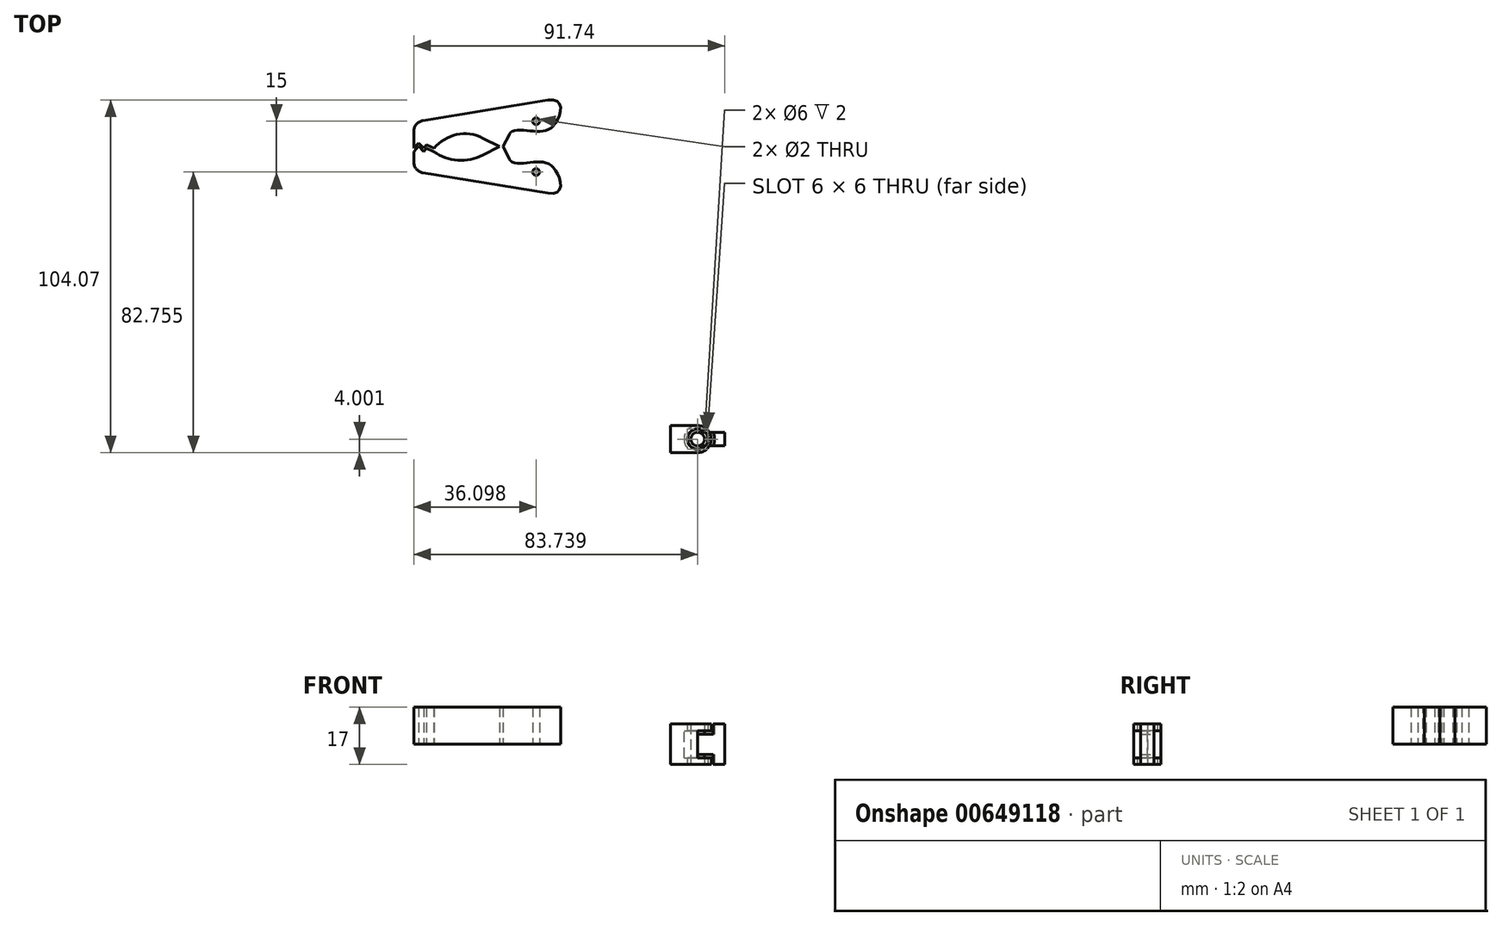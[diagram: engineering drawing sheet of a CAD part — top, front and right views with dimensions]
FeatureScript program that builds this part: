
annotation { "Feature Type Name" : "Feature", "Feature Type Description" : "" }
export const myFeature = defineFeature(function(context is Context, id is Id, definition is map)
    precondition{}
    {
        {
            var Q0;
            Q0=qCreatedBy(makeId("Top.planeOp"),FACE);
            var sketch = newSketch(context, id + "F0", { "sketchPlane" : qUnion([Q0])});
            skLineSegment(sketch, "E0.left", {"start": v(-16.53, 12.52) * mm, "end": v(-16.53, 12.52) * mm});
            skLineSegment(sketch, "E0.right", {"start": v(-56.54, 60.56) * mm, "end": v(-56.54, 63.56) * mm});
            skPoint(sketch, "E0.middle", {"position": v(-33.55, 63.83) * mm});
            skLineSegment(sketch, "E1.top", {"start": v(-56.54, 58.56) * mm, "end": v(-50.54, 58.56) * mm, "construction": true});
            skLineSegment(sketch, "E1.left", {"start": v(-56.54, 60.56) * mm, "end": v(-56.54, 58.56) * mm});
            skLineSegment(sketch, "E1.right", {"start": v(-56.53, 8.52) * mm, "end": v(-56.53, 8.52) * mm});
            skLineSegment(sketch, "E2", {"start": v(-53.54, 58.56) * mm, "end": v(-55.11, 60.19) * mm});
            skPoint(sketch, "E3.visualSharp", {"position": v(-50.54, 60.56) * mm});
            skPoint(sketch, "E4.visualSharp", {"position": v(-56.54, 65.45) * mm});
            skArc(sketch, "E4.filletArc", {"start": v(-53.81, 66.77) * mm, "mid": v(-55.77, 65.67) * mm, "end": v(-56.54, 63.56) * mm});
            skPoint(sketch, "E5.visualSharp", {"position": v(-10.57, 67.1) * mm});
            skPoint(sketch, "E6.visualSharp", {"position": v(-10.57, 62.2) * mm});
            skLineSegment(sketch, "E7", {"start": v(-33.55, 63.83) * mm, "end": v(-16.68, 69.92) * mm, "construction": true});
            skCircle(sketch, "E8", {"center": v(-20.44, 68.56) * mm, "radius": 1 * mm, "construction": true});
            skLineSegment(sketch, "E9", {"start": v(-36.15, 61.59) * mm, "end": v(-31.23, 59.06) * mm});
            skLineSegment(sketch, "E10", {"start": v(-31.23, 59.06) * mm, "end": v(-30.23, 59.06) * mm, "construction": true});
            skLineSegment(sketch, "E11", {"start": v(-30.23, 59.06) * mm, "end": v(-28.36, 62.7) * mm});
            skLineSegment(sketch, "E12", {"start": v(-62.4, 59.06) * mm, "end": v(9.99, 59.06) * mm, "construction": true});
            skLineSegment(sketch, "E13.MirrorCS", {"start": v(-30.23, 59.06) * mm, "end": v(-28.36, 55.42) * mm});
            skCircle(sketch, "E14.MirrorC", {"center": v(-20.44, 49.56) * mm, "radius": 1 * mm, "construction": true});
            skArc(sketch, "E15.MirrorCS", {"start": v(-53.81, 51.36) * mm, "mid": v(-55.77, 52.46) * mm, "end": v(-56.54, 54.56) * mm});
            skLineSegment(sketch, "E16.MirrorCS", {"start": v(-56.54, 57.56) * mm, "end": v(-56.54, 54.56) * mm});
            skLineSegment(sketch, "E17.MirrorCS", {"start": v(-33.55, 54.3) * mm, "end": v(-16.68, 48.2) * mm, "construction": true});
            skPoint(sketch, "E18.MirrorP", {"position": v(-10.57, 55.92) * mm});
            skPoint(sketch, "E19.MirrorP", {"position": v(-10.57, 51.04) * mm});
            skPoint(sketch, "E20.MirrorP", {"position": v(-56.54, 52.68) * mm});
            skPoint(sketch, "E21.MirrorP", {"position": v(-50.54, 57.56) * mm});
            skPoint(sketch, "E22.visualSharp", {"position": v(-33.21, 60.08) * mm});
            skPoint(sketch, "E23.visualSharp", {"position": v(-33.21, 58.05) * mm});
            skPoint(sketch, "E24.visualSharp", {"position": v(-28.21, 55.13) * mm});
            skArc(sketch, "E24.filletArc", {"start": v(-28.36, 55.42) * mm, "mid": v(-28, 54.93) * mm, "end": v(-27.51, 54.56) * mm});
            skPoint(sketch, "E25.visualSharp", {"position": v(-28.21, 63) * mm});
            skArc(sketch, "E25.filletArc", {"start": v(-27.51, 63.56) * mm, "mid": v(-28, 63.2) * mm, "end": v(-28.36, 62.7) * mm});
            skLineSegment(sketch, "E26", {"start": v(-56.54, 60.56) * mm, "end": v(-49.14, 58.6) * mm, "construction": true});
            skLineSegment(sketch, "E27", {"start": v(-56.54, 58.56) * mm, "end": v(-55.11, 60.19) * mm});
            skLineSegment(sketch, "E28", {"start": v(-53.54, 58.56) * mm, "end": v(-52.84, 59.59) * mm});
            skLineSegment(sketch, "E29", {"start": v(-52.84, 59.59) * mm, "end": v(-50.54, 58.56) * mm});
            skLineSegment(sketch, "E30.top", {"start": v(-56.54, 57.56) * mm, "end": v(-50.54, 57.56) * mm, "construction": true});
            skLineSegment(sketch, "E31", {"start": v(-53.54, 57.56) * mm, "end": v(-55.11, 59.19) * mm});
            skPoint(sketch, "E32.visualSharp", {"position": v(-50.53, 48.52) * mm});
            skLineSegment(sketch, "E33", {"start": v(-56.58, 59.56) * mm, "end": v(-49.08, 57.64) * mm, "construction": true});
            skLineSegment(sketch, "E34", {"start": v(-56.54, 57.56) * mm, "end": v(-55.11, 59.19) * mm});
            skLineSegment(sketch, "E35", {"start": v(-53.54, 57.56) * mm, "end": v(-52.83, 58.6) * mm});
            skLineSegment(sketch, "E36", {"start": v(-52.83, 58.6) * mm, "end": v(-50.65, 57.61) * mm});
            skLineSegment(sketch, "E37", {"start": v(-56.58, 59.56) * mm, "end": v(-56.54, 57.56) * mm, "construction": true});
            skArc(sketch, "E38", {"start": v(-36.15, 61.59) * mm, "mid": v(-43.88, 62.63) * mm, "end": v(-50.54, 58.56) * mm});
            skLineSegment(sketch, "E39", {"start": v(-53.81, 66.77) * mm, "end": v(-17, 72.78) * mm});
            skLineSegment(sketch, "E40.MirrorCS", {"start": v(-53.81, 51.36) * mm, "end": v(-17, 45.35) * mm});
            skLineSegment(sketch, "E41.MirrorCS", {"start": v(-17, 45.35) * mm, "end": v(-17, 45.35) * mm});
            skLineSegment(sketch, "E42.MirrorCS", {"start": v(-36.15, 56.54) * mm, "end": v(-31.23, 59.06) * mm});
            skArc(sketch, "E43", {"start": v(-50.65, 57.61) * mm, "mid": v(-43.55, 55.04) * mm, "end": v(-36.15, 56.54) * mm});
            skLineSegment(sketch, "E44", {"start": v(-20.44, 68.56) * mm, "end": v(-20.44, 49.56) * mm, "construction": true});
            skCircle(sketch, "E45", {"center": v(-20.44, 66.56) * mm, "radius": 1 * mm});
            skFitSpline(sketch, "E46", {"points": [v(-27.51, 63.56) * mm, v(-20.44, 63.56) * mm, v(-14.5, 66.38) * mm, v(-17, 72.78) * mm], "startDerivative": vector(15.1, 7.97) * mm, "endDerivative": vector(-45.53, -7.44) * mm});
            skFitSpline(sketch, "E47.MirrorCS", {"points": [v(-27.51, 54.56) * mm, v(-20.44, 54.56) * mm, v(-14.5, 51.75) * mm, v(-17, 45.35) * mm], "startDerivative": vector(15.1, -7.97) * mm, "endDerivative": vector(-45.53, 7.44) * mm});
            skCircle(sketch, "E48.MirrorC", {"center": v(-20.44, 51.56) * mm, "radius": 1 * mm});
            skSolve(sketch);
        }
        {
            var Q0;
            Q0=makeQuery(id+"F0.imprint","IMPRINT",FACE,{"disambiguationData":[TD([[makeQuery(id+"F0.imprint","IMPRINT",EDGE,{"derivedFrom":sQuery(id+"F0.wireOp",EDGE,"E0.right")}),-1.0]])]});
            extrude(context, id + "F1", {"entities" : qUnion([Q0]), "depth" : 11 * mm, "offsetDistance" : 25 * mm});
        }
        {
            var Q0;
            Q0=qCreatedBy(makeId("Top.planeOp"),FACE);
            var sketch = newSketch(context, id + "F2", { "sketchPlane" : qUnion([Q0])});
            skLineSegment(sketch, "E49.bottom", {"start": v(-19.85, -51.8) * mm, "end": v(-33.85, -51.8) * mm, "construction": true});
            skLineSegment(sketch, "E49.left", {"start": v(-19.85, -51.8) * mm, "end": v(-19.85, -5.8) * mm, "construction": true});
            skLineSegment(sketch, "E49.right", {"start": v(-33.85, -51.8) * mm, "end": v(-33.85, -5.8) * mm, "construction": true});
            skPoint(sketch, "E49.middle", {"position": v(-26.85, -28.8) * mm});
            skCircle(sketch, "E50", {"center": v(-26.85, -25) * mm, "radius": 2 * mm});
            skCircle(sketch, "E51", {"center": v(-26.85, -25) * mm, "radius": 2.1 * mm});
            skCircle(sketch, "E52", {"center": v(-26.85, -25) * mm, "radius": 3.1 * mm});
            skCircle(sketch, "E53", {"center": v(-26.85, -25) * mm, "radius": 3 * mm});
            skCircle(sketch, "E54", {"center": v(-26.85, -25) * mm, "radius": 3.2 * mm, "construction": true});
            skLineSegment(sketch, "E55", {"start": v(-26.85, -21.9) * mm, "end": v(-26.85, -21.8) * mm});
            skLineSegment(sketch, "E56", {"start": v(-26.85, -21.8) * mm, "end": v(-26.78, -28.1) * mm});
            skLineSegment(sketch, "E57", {"start": v(-26.78, -28.1) * mm, "end": v(-26.78, -28.2) * mm});
            skArc(sketch, "E58", {"start": v(-26.78, -28.2) * mm, "mid": v(-23.66, -24.97) * mm, "end": v(-26.85, -21.8) * mm});
            skLineSegment(sketch, "E59", {"start": v(-26.85, -21.8) * mm, "end": v(-26.85, -5.8) * mm, "construction": true});
            skLineSegment(sketch, "E60.bottom", {"start": v(-25.85, -51.8) * mm, "end": v(-27.85, -51.8) * mm, "construction": true});
            skLineSegment(sketch, "E60.top", {"start": v(-25.85, -43.8) * mm, "end": v(-27.85, -43.8) * mm, "construction": true});
            skLineSegment(sketch, "E60.left", {"start": v(-27.85, -51.8) * mm, "end": v(-27.85, -43.8) * mm, "construction": true});
            skLineSegment(sketch, "E60.right", {"start": v(-25.85, -51.8) * mm, "end": v(-25.85, -43.8) * mm, "construction": true});
            skPoint(sketch, "E60.middle", {"position": v(-26.85, -47.8) * mm});
            skLineSegment(sketch, "E61.bottom", {"start": v(-19.85, -21.8) * mm, "end": v(-33.85, -21.8) * mm, "construction": true});
            skLineSegment(sketch, "E61.left", {"start": v(-19.85, -21.8) * mm, "end": v(-19.85, -5.8) * mm, "construction": true});
            skPoint(sketch, "E61.middle", {"position": v(-26.85, -13.8) * mm});
            skLineSegment(sketch, "E62", {"start": v(-37.85, -11.8) * mm, "end": v(-33.85, -11.8) * mm, "construction": true});
            skLineSegment(sketch, "E63", {"start": v(-41.85, -11.8) * mm, "end": v(-37.85, -11.8) * mm, "construction": true});
            skLineSegment(sketch, "E64", {"start": v(-15.85, -11.8) * mm, "end": v(-11.85, -11.8) * mm, "construction": true});
            skLineSegment(sketch, "E65", {"start": v(-19.85, -11.8) * mm, "end": v(-15.85, -11.8) * mm, "construction": true});
            skCircle(sketch, "E66", {"center": v(-37.85, -11.8) * mm, "radius": 1 * mm});
            skCircle(sketch, "E67", {"center": v(-15.85, -11.8) * mm, "radius": 1 * mm});
            skLineSegment(sketch, "E68", {"start": v(-26.85, -43.8) * mm, "end": v(-26.85, -51.8) * mm, "construction": true});
            skLineSegment(sketch, "E69", {"start": v(-33.85, -11.8) * mm, "end": v(-19.85, -11.8) * mm, "construction": true});
            skLineSegment(sketch, "E70.bottom", {"start": v(-33.85, -5.8) * mm, "end": v(-41.85, -5.8) * mm});
            skLineSegment(sketch, "E70.top", {"start": v(-33.85, -51.8) * mm, "end": v(-41.85, -51.8) * mm, "construction": true});
            skLineSegment(sketch, "E70.left", {"start": v(-33.85, -5.8) * mm, "end": v(-33.85, -51.8) * mm, "construction": true});
            skLineSegment(sketch, "E70.right", {"start": v(-41.85, -5.8) * mm, "end": v(-41.85, -51.8) * mm, "construction": true});
            skLineSegment(sketch, "E71.bottom", {"start": v(-19.85, -5.8) * mm, "end": v(-11.85, -5.8) * mm});
            skLineSegment(sketch, "E71.top", {"start": v(-19.85, -52.05) * mm, "end": v(-11.85, -52.05) * mm, "construction": true});
            skLineSegment(sketch, "E71.left", {"start": v(-19.85, -5.8) * mm, "end": v(-19.85, -52.05) * mm, "construction": true});
            skLineSegment(sketch, "E71.right", {"start": v(-11.85, -5.8) * mm, "end": v(-11.85, -52.05) * mm, "construction": true});
            skLineSegment(sketch, "E72", {"start": v(-26.85, -28.8) * mm, "end": v(-26.85, -43.8) * mm, "construction": true});
            skLineSegment(sketch, "E73", {"start": v(-27.85, -51.8) * mm, "end": v(-25.85, -51.8) * mm});
            skLineSegment(sketch, "E74", {"start": v(-25.85, -51.8) * mm, "end": v(-27.85, -49.8) * mm});
            skLineSegment(sketch, "E75", {"start": v(-27.85, -49.8) * mm, "end": v(-25.85, -49.8) * mm});
            skLineSegment(sketch, "E76", {"start": v(-25.85, -49.8) * mm, "end": v(-27.85, -47.8) * mm});
            skLineSegment(sketch, "E77", {"start": v(-27.85, -47.8) * mm, "end": v(-25.85, -47.8) * mm});
            skLineSegment(sketch, "E78", {"start": v(-25.85, -47.8) * mm, "end": v(-27.85, -48.1) * mm});
            skArc(sketch, "E79", {"start": v(-41.85, -37.8) * mm, "mid": v(-37.75, -47.7) * mm, "end": v(-27.85, -51.8) * mm});
            skArc(sketch, "E80", {"start": v(-25.85, -51.8) * mm, "mid": v(-15.96, -47.7) * mm, "end": v(-11.85, -37.8) * mm});
            skLineSegment(sketch, "E81", {"start": v(-41.85, -37.8) * mm, "end": v(-11.85, -37.8) * mm, "construction": true});
            skLineSegment(sketch, "E82", {"start": v(-41.85, -37.8) * mm, "end": v(-41.85, -5.8) * mm});
            skLineSegment(sketch, "E83", {"start": v(-11.85, -37.8) * mm, "end": v(-11.85, -5.8) * mm});
            skLineSegment(sketch, "E84", {"start": v(-33.85, -5.8) * mm, "end": v(-33.85, -21.8) * mm});
            skLineSegment(sketch, "E85", {"start": v(-19.85, -28.48) * mm, "end": v(-19.85, -47.8) * mm});
            skLineSegment(sketch, "E86", {"start": v(-19.85, -47.8) * mm, "end": v(-25.85, -47.8) * mm});
            skLineSegment(sketch, "E87", {"start": v(-19.85, -21.8) * mm, "end": v(-19.85, -5.8) * mm});
            skLineSegment(sketch, "E88", {"start": v(-27.85, -47.8) * mm, "end": v(-33.85, -47.8) * mm});
            skLineSegment(sketch, "E89", {"start": v(-33.85, -47.8) * mm, "end": v(-33.85, -21.8) * mm});
            skLineSegment(sketch, "E90", {"start": v(-33.85, -21.66) * mm, "end": v(-33.88, -21.7) * mm});
            skLineSegment(sketch, "E91", {"start": v(-19.85, -21.8) * mm, "end": v(-26.84, -23) * mm});
            skLineSegment(sketch, "E92", {"start": v(-26.8, -27) * mm, "end": v(-19.85, -28.48) * mm});
            skLineSegment(sketch, "E93", {"start": v(-26.85, -21.9) * mm, "end": v(-33.85, -21.38) * mm});
            skLineSegment(sketch, "E94", {"start": v(-26.78, -28.1) * mm, "end": v(-33.85, -28.8) * mm});
            skLineSegment(sketch, "E95", {"start": v(-26.85, -25) * mm, "end": v(-19.85, -25) * mm, "construction": true});
            skLineSegment(sketch, "E96", {"start": v(-26.85, -25) * mm, "end": v(-33.85, -25) * mm, "construction": true});
            skLineSegment(sketch, "E97", {"start": v(-33.85, -5.8) * mm, "end": v(-26.85, -5.8) * mm, "construction": true});
            skLineSegment(sketch, "E98", {"start": v(-26.85, -5.8) * mm, "end": v(-19.85, -5.8) * mm, "construction": true});
            skLineSegment(sketch, "E99", {"start": v(-26.85, -25) * mm, "end": v(-26.85, -28.8) * mm, "construction": true});
            skLineSegment(sketch, "E100.bottom", {"start": v(13.2, -7.21) * mm, "end": v(19.2, -7.21) * mm, "construction": true});
            skLineSegment(sketch, "E100.top", {"start": v(13.2, -53.95) * mm, "end": v(19.2, -53.95) * mm, "construction": true});
            skLineSegment(sketch, "E100.left", {"start": v(13.2, -7.21) * mm, "end": v(13.2, -53.95) * mm, "construction": true});
            skLineSegment(sketch, "E100.right", {"start": v(19.2, -7.21) * mm, "end": v(19.2, -53.95) * mm, "construction": true});
            skLineSegment(sketch, "E101", {"start": v(13.2, -13.21) * mm, "end": v(19.2, -13.21) * mm, "construction": true});
            skCircle(sketch, "E102", {"center": v(16.2, -13.21) * mm, "radius": 1 * mm});
            skCircle(sketch, "E103", {"center": v(27.2, -27.19) * mm, "radius": 2 * mm});
            skCircle(sketch, "E104", {"center": v(27.2, -27.19) * mm, "radius": 3 * mm});
            skCircle(sketch, "E105", {"center": v(27.2, -27.19) * mm, "radius": 4 * mm});
            skCircle(sketch, "E106", {"center": v(27.2, -27.19) * mm, "radius": 5 * mm});
            skLineSegment(sketch, "E107", {"start": v(27.2, -27.19) * mm, "end": v(19.2, -27.19) * mm, "construction": true});
            skLineSegment(sketch, "E108", {"start": v(27.2, -7.21) * mm, "end": v(27.2, -54.3) * mm, "construction": true});
            skPoint(sketch, "E108.startSnap0", {"position": v(16.2, -7.21) * mm});
            skLineSegment(sketch, "E109.MirrorCS", {"start": v(35.2, -7.21) * mm, "end": v(35.2, -53.95) * mm, "construction": true});
            skLineSegment(sketch, "E110.MirrorCS", {"start": v(41.2, -13.21) * mm, "end": v(35.2, -13.21) * mm, "construction": true});
            skLineSegment(sketch, "E111.MirrorCS", {"start": v(41.2, -7.21) * mm, "end": v(41.2, -53.95) * mm, "construction": true});
            skLineSegment(sketch, "E112.MirrorCS", {"start": v(41.2, -7.21) * mm, "end": v(35.2, -7.21) * mm, "construction": true});
            skCircle(sketch, "E113.MirrorC", {"center": v(38.2, -13.21) * mm, "radius": 1 * mm});
            skLineSegment(sketch, "E114.MirrorCS", {"start": v(41.2, -53.95) * mm, "end": v(35.2, -53.95) * mm, "construction": true});
            skLineSegment(sketch, "E115.MirrorCS", {"start": v(27.2, -27.19) * mm, "end": v(35.2, -27.19) * mm, "construction": true});
            skLineSegment(sketch, "E116", {"start": v(27.2, -25.19) * mm, "end": v(35.2, -25.19) * mm});
            skLineSegment(sketch, "E117.MirrorCS", {"start": v(27.2, -29.19) * mm, "end": v(35.2, -29.19) * mm});
            skLineSegment(sketch, "E118", {"start": v(19.2, -23.19) * mm, "end": v(19.2, -31.19) * mm});
            skLineSegment(sketch, "E119", {"start": v(35.2, -25.19) * mm, "end": v(35.2, -29.19) * mm});
            skLineSegment(sketch, "E120", {"start": v(23.2, -27.19) * mm, "end": v(25.2, -27.19) * mm});
            skLineSegment(sketch, "E121", {"start": v(27.2, -23.19) * mm, "end": v(19.2, -23.19) * mm});
            skLineSegment(sketch, "E122", {"start": v(27.2, -31.19) * mm, "end": v(19.2, -31.19) * mm});
            skSolve(sketch);
        }
        {
            var Q0;
            {var subQ5=sQuery(id+"F2.wireOp",EDGE,"E118");Q0=makeQuery(id+"F2.imprint","IMPRINT",FACE,{"disambiguationData":[TD([[makeQuery(id+"F2.imprint","IMPRINT",EDGE,{"derivedFrom":subQ5}),1.0]])]});}
            var Q1;
            {var subQ0=sQuery(id+"F2.wireOp",EDGE,"B579V9jg-vVpn-PewL-seOk-HfGn0jfsSapa");var subQ1=sQuery(id+"F2.wireOp",EDGE,"E105");var subQ2=makeQuery(id+"F2.imprint","INTERSECT",VERTEX,{"derivedFrom":[subQ1,subQ0]});Q1=makeQuery(id+"F2.imprint","IMPRINT",FACE,{"disambiguationData":[TD([[makeQuery(id+"F2.imprint","IMPRINT",EDGE,{"disambiguationData":[TD([[subQ2,-1.0]])],"derivedFrom":subQ1}),1.0]])]});}
            var Q2;
            {var subQ5=sQuery(id+"F2.wireOp",EDGE,"E116");var subQ7=sQuery(id+"F2.wireOp",EDGE,"E104");var subQ8=makeQuery(id+"F2.imprint","INTERSECT",VERTEX,{"derivedFrom":[subQ7,subQ5]});Q2=makeQuery(id+"F2.imprint","IMPRINT",FACE,{"disambiguationData":[TD([[makeQuery(id+"F2.imprint","IMPRINT",EDGE,{"disambiguationData":[TD([[subQ8,-1.0]])],"derivedFrom":subQ7}),-1.0]])]});}
            var Q3;
            {var subQ0=sQuery(id+"F2.wireOp",EDGE,"E120");Q3=makeQuery(id+"F2.imprint","IMPRINT",FACE,{"disambiguationData":[TD([[makeQuery(id+"F2.imprint","IMPRINT",EDGE,{"derivedFrom":subQ0}),-1.0]])]});}
            var Q4;
            {var subQ0=sQuery(id+"F2.wireOp",EDGE,"E103");var subQ1=makeQuery(id+"F2.imprint","INTERSECT",VERTEX,{"derivedFrom":[subQ0,sQuery(id+"F2.wireOp",EDGE,"E116")]});Q4=makeQuery(id+"F2.imprint","IMPRINT",FACE,{"disambiguationData":[TD([[makeQuery(id+"F2.imprint","IMPRINT",EDGE,{"disambiguationData":[TD([[subQ1,-1.0]])],"derivedFrom":subQ0}),1.0]])]});}
            var Q5;
            {var subQ0=sQuery(id+"F2.wireOp",EDGE,"E105");var subQ8=makeQuery(id+"F2.imprint","INTERSECT",VERTEX,{"derivedFrom":[subQ0,sQuery(id+"F2.wireOp",EDGE,"E120")]});Q5=makeQuery(id+"F2.imprint","IMPRINT",FACE,{"disambiguationData":[TD([[makeQuery(id+"F2.imprint","IMPRINT",EDGE,{"disambiguationData":[TD([[subQ8,1.0]])],"derivedFrom":subQ0}),-1.0]])]});}
            var Q6;
            {var subQ0=sQuery(id+"F2.wireOp",EDGE,"E116");var subQ1=sQuery(id+"F2.wireOp",EDGE,"E104");var subQ2=makeQuery(id+"F2.imprint","INTERSECT",VERTEX,{"derivedFrom":[subQ1,subQ0]});Q6=makeQuery(id+"F2.imprint","IMPRINT",FACE,{"disambiguationData":[TD([[makeQuery(id+"F2.imprint","IMPRINT",EDGE,{"disambiguationData":[TD([[subQ2,1.0]])],"derivedFrom":subQ1}),-1.0]])]});}
            extrude(context, id + "F3", {"entities" : qUnion([Q0, Q1, Q2, Q3, Q4, Q5, Q6]), "endBound" : BoundingType.SYMMETRIC, "depth" : 12 * mm, "offsetDistance" : 25 * mm});
        }
        {
            var Q0;
            {var subQ4=sQuery(id+"F2.wireOp",EDGE,"E104");var subQ8=makeQuery(id+"F2.imprint","INTERSECT",VERTEX,{"derivedFrom":[subQ4,sQuery(id+"F2.wireOp",EDGE,"E120")]});Q0=makeQuery(id+"F2.imprint","IMPRINT",FACE,{"disambiguationData":[TD([[makeQuery(id+"F2.imprint","IMPRINT",EDGE,{"disambiguationData":[TD([[subQ8,1.0]])],"derivedFrom":subQ4}),-1.0]])]});}
            var Q1;
            {var subQ0=sQuery(id+"F2.wireOp",EDGE,"E116");var subQ1=sQuery(id+"F2.wireOp",EDGE,"E104");var subQ2=makeQuery(id+"F2.imprint","INTERSECT",VERTEX,{"derivedFrom":[subQ1,subQ0]});Q1=makeQuery(id+"F2.imprint","IMPRINT",FACE,{"disambiguationData":[TD([[makeQuery(id+"F2.imprint","IMPRINT",EDGE,{"disambiguationData":[TD([[subQ2,1.0]])],"derivedFrom":subQ1}),-1.0]])]});}
            var Q2;
            {var subQ0=sQuery(id+"F2.wireOp",EDGE,"E120");var subQ1=sQuery(id+"F2.wireOp",EDGE,"E104");var subQ2=makeQuery(id+"F2.imprint","INTERSECT",VERTEX,{"derivedFrom":[subQ1,subQ0]});Q2=makeQuery(id+"F2.imprint","IMPRINT",FACE,{"disambiguationData":[TD([[makeQuery(id+"F2.imprint","IMPRINT",EDGE,{"disambiguationData":[TD([[subQ2,-1.0]])],"derivedFrom":subQ1}),-1.0]])]});}
            extrude(context, id + "F4", {"entities" : qUnion([Q0, Q1, Q2]), "operationType" : NewBodyOperationType.REMOVE, "endBound" : BoundingType.SYMMETRIC, "oppositeDirection" : true, "depth" : 8 * mm, "offsetDistance" : 25 * mm});
        }
        {
            var Q0;
            {var subQ0=sQuery(id+"F2.wireOp",EDGE,"E116");var subQ1=sQuery(id+"F2.wireOp",EDGE,"E103");var subQ2=makeQuery(id+"F2.imprint","INTERSECT",VERTEX,{"derivedFrom":[subQ1,subQ0]});Q0=makeQuery(id+"F2.imprint","IMPRINT",FACE,{"disambiguationData":[TD([[makeQuery(id+"F2.imprint","IMPRINT",EDGE,{"disambiguationData":[TD([[subQ2,1.0]])],"derivedFrom":subQ1}),-1.0]])]});}
            var Q1;
            {var subQ0=sQuery(id+"F2.wireOp",EDGE,"E116");var subQ1=sQuery(id+"F2.wireOp",EDGE,"E105");var subQ2=makeQuery(id+"F2.imprint","INTERSECT",VERTEX,{"derivedFrom":[subQ1,subQ0]});Q1=makeQuery(id+"F2.imprint","IMPRINT",FACE,{"disambiguationData":[TD([[makeQuery(id+"F2.imprint","IMPRINT",EDGE,{"disambiguationData":[TD([[subQ2,1.0]])],"derivedFrom":subQ1}),-1.0]])]});}
            var Q2;
            {var subQ0=sQuery(id+"F2.wireOp",EDGE,"E116");var subQ1=sQuery(id+"F2.wireOp",EDGE,"E104");var subQ2=makeQuery(id+"F2.imprint","INTERSECT",VERTEX,{"derivedFrom":[subQ1,subQ0]});Q2=makeQuery(id+"F2.imprint","IMPRINT",FACE,{"disambiguationData":[TD([[makeQuery(id+"F2.imprint","IMPRINT",EDGE,{"disambiguationData":[TD([[subQ2,1.0]])],"derivedFrom":subQ1}),-1.0]])]});}
            extrude(context, id + "F5", {"entities" : qUnion([Q0, Q1, Q2]), "operationType" : NewBodyOperationType.ADD, "endBound" : BoundingType.SYMMETRIC, "depth" : 6 * mm, "offsetDistance" : 25 * mm});
        }
        {
            var Q0;
            {var subQ5=sQuery(id+"F2.wireOp",EDGE,"E119");Q0=makeQuery(id+"F2.imprint","IMPRINT",FACE,{"disambiguationData":[TD([[makeQuery(id+"F2.imprint","IMPRINT",EDGE,{"derivedFrom":subQ5}),-1.0]])]});}
            extrude(context, id + "F6", {"entities" : qUnion([Q0]), "operationType" : NewBodyOperationType.ADD, "endBound" : BoundingType.SYMMETRIC, "depth" : 12 * mm, "offsetDistance" : 25 * mm});
        }
    });
